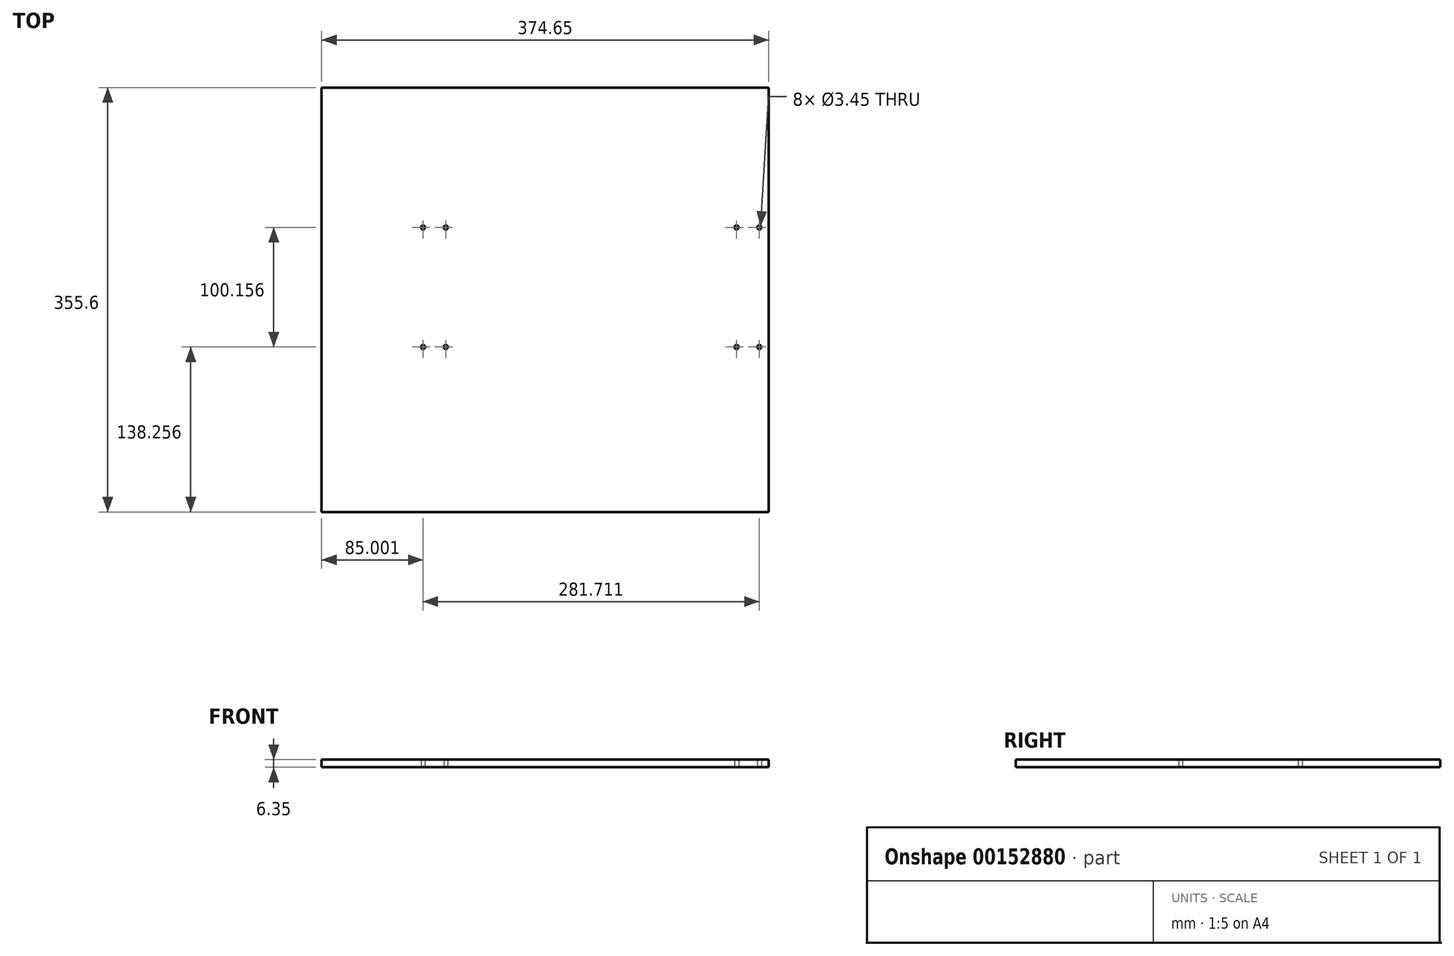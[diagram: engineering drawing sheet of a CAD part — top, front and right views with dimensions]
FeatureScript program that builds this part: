
annotation { "Feature Type Name" : "Feature", "Feature Type Description" : "" }
export const myFeature = defineFeature(function(context is Context, id is Id, definition is map)
    precondition{}
    {
        {
            var Q0;
            Q0=qCreatedBy(makeId("Top.planeOp"),FACE);
            var sketch = newSketch(context, id + "F0", { "sketchPlane" : qUnion([Q0])});
            skLineSegment(sketch, "E0.bottom", {"start": v(0, 0) * mm, "end": v(374.65, 0) * mm});
            skLineSegment(sketch, "E0.top", {"start": v(0, -355.6) * mm, "end": v(374.65, -355.6) * mm});
            skLineSegment(sketch, "E0.left", {"start": v(0, 0) * mm, "end": v(0, -355.6) * mm});
            skLineSegment(sketch, "E0.right", {"start": v(374.65, 0) * mm, "end": v(374.65, -355.6) * mm});
            skLineSegment(sketch, "E1.bottom", {"start": v(104.05, -117.19) * mm, "end": v(104.05, -217.34) * mm, "construction": true});
            skLineSegment(sketch, "E1.top", {"start": v(85, -117.19) * mm, "end": v(85, -217.34) * mm, "construction": true});
            skLineSegment(sketch, "E1.left", {"start": v(104.05, -117.19) * mm, "end": v(85, -117.19) * mm, "construction": true});
            skLineSegment(sketch, "E1.right", {"start": v(104.05, -217.34) * mm, "end": v(85, -217.34) * mm, "construction": true});
            skPoint(sketch, "E1.middle", {"position": v(94.53, -167.27) * mm});
            skCircle(sketch, "E2", {"center": v(85, -217.34) * mm, "radius": 1.73 * mm});
            skCircle(sketch, "E3", {"center": v(104.05, -217.34) * mm, "radius": 1.73 * mm});
            skCircle(sketch, "E4", {"center": v(85, -117.19) * mm, "radius": 1.73 * mm});
            skCircle(sketch, "E5", {"center": v(104.05, -117.19) * mm, "radius": 1.73 * mm});
            skLineSegment(sketch, "E6", {"start": v(94.53, -167.27) * mm, "end": v(0, -167.27) * mm, "construction": true});
            skLineSegment(sketch, "E7", {"start": v(374.65, -167.27) * mm, "end": v(357.19, -167.27) * mm, "construction": true});
            skLineSegment(sketch, "E8.bottom", {"start": v(347.66, -117.19) * mm, "end": v(366.71, -117.19) * mm, "construction": true});
            skLineSegment(sketch, "E8.top", {"start": v(347.66, -217.34) * mm, "end": v(366.71, -217.34) * mm, "construction": true});
            skLineSegment(sketch, "E8.left", {"start": v(347.66, -117.19) * mm, "end": v(347.66, -217.34) * mm, "construction": true});
            skLineSegment(sketch, "E8.right", {"start": v(366.71, -117.19) * mm, "end": v(366.71, -217.34) * mm, "construction": true});
            skPoint(sketch, "E8.middle", {"position": v(357.19, -167.27) * mm});
            skCircle(sketch, "E9", {"center": v(347.66, -117.19) * mm, "radius": 1.73 * mm});
            skCircle(sketch, "E10", {"center": v(366.71, -117.19) * mm, "radius": 1.73 * mm});
            skCircle(sketch, "E11", {"center": v(366.71, -217.34) * mm, "radius": 1.73 * mm});
            skCircle(sketch, "E12", {"center": v(347.66, -217.34) * mm, "radius": 1.73 * mm});
            skLineSegment(sketch, "E13", {"start": v(366.71, -217.34) * mm, "end": v(366.71, -355.6) * mm, "construction": true});
            skSolve(sketch);
        }
        {
            var Q0;
            Q0 = qSketchRegion(id + "F0", true);
            extrude(context, id + "F1", {"entities" : qUnion([Q0]), "depth" : 6.35 * mm});
        }
    });
